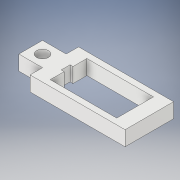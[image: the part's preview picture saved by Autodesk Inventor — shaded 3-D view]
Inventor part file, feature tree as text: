
AUTODESK INVENTOR PART (.ipt)
format: ipt  version: 2019 (Build 230136000, 136)  size: 174,080 bytes
history: native  units: in
note: dims shown in document units (in); Inventor stores cm internally (conversion verified against a paired STEP export)
features: sketch x4, extrude x3, plane x2
ambient origin geometry x8: Origin, YZ Plane, XZ Plane, XY Plane, X Axis, Y Axis, Z Axis, Center Point
bodies: Solid14 (feature_tree)
feature tree (9):
  plane  "Work Plane1"
  sketch  "Sketch1"  dims[d17=0.1969in d18=0.0in d19=0.4882in]
  plane  "Work Plane3"
  extrude  "Extrusion4"  Depth=0.4882in
  extrude  "Extrusion5"  Depth=0.1181in
  extrude  "Extrusion6"  Depth=0.315in
  sketch  "Sketch6"  dims[d20=0.0394in d21=0.1181in]
  sketch  "Sketch7"  dims[d22=0.1969in d23=0.0in d24=0.315in]
  sketch  "Sketch8"  dims[d25=0.315in d26=0.1575in d27=0.1969in d28=0.0in]
